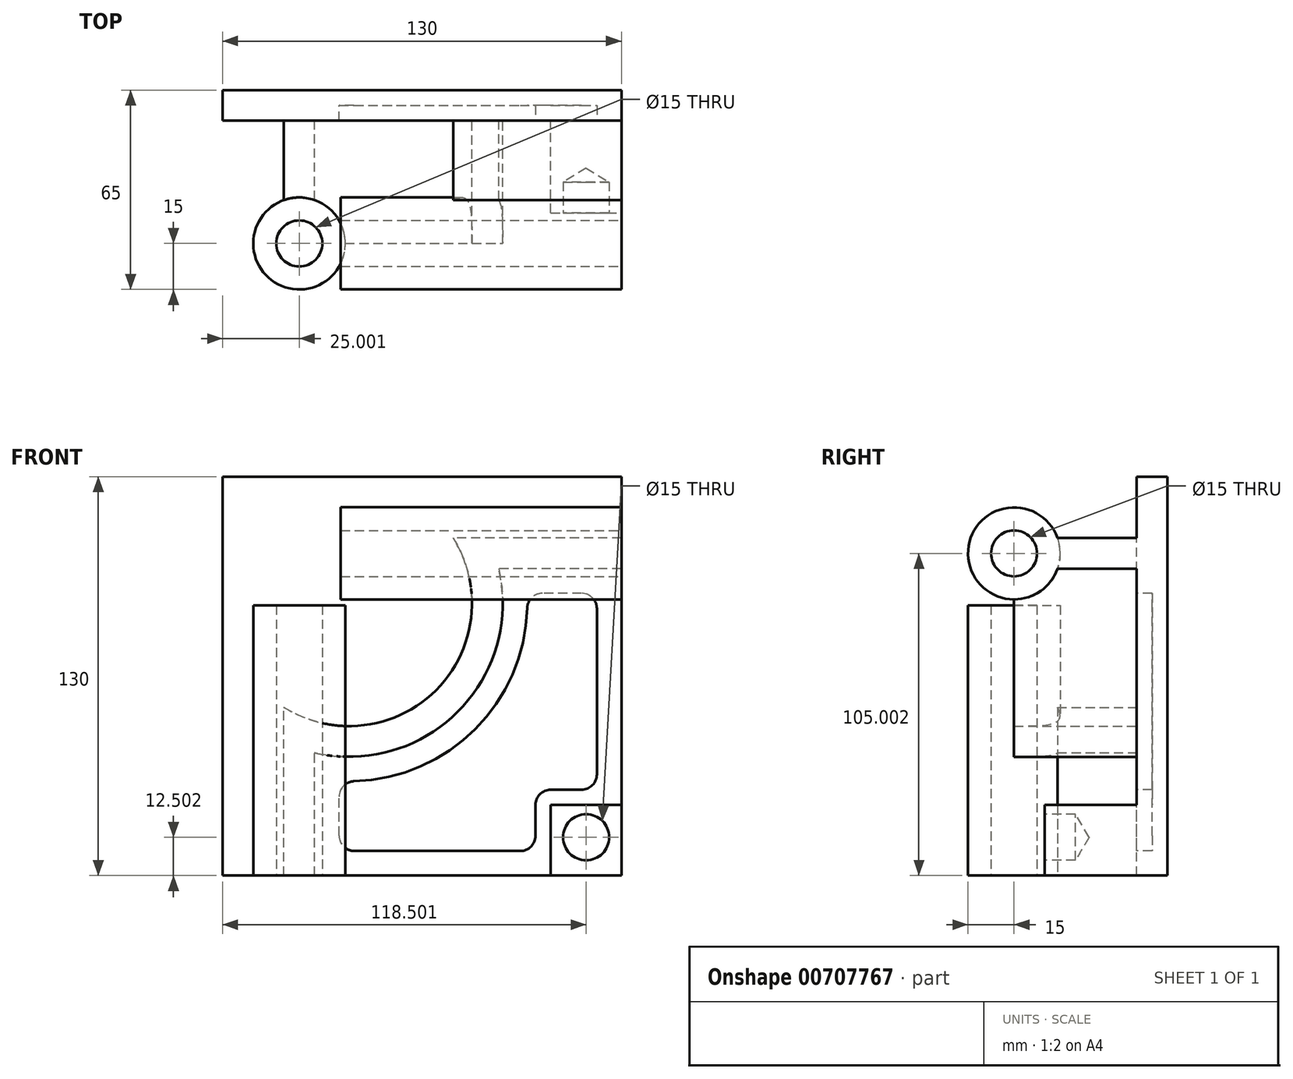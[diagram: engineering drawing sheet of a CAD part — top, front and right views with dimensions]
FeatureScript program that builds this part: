
annotation { "Feature Type Name" : "Feature", "Feature Type Description" : "" }
export const myFeature = defineFeature(function(context is Context, id is Id, definition is map)
    precondition{}
    {
        {
            var Q0;
            Q0=qCreatedBy(makeId("Front.planeOp"),FACE);
            var sketch = newSketch(context, id + "F0", { "sketchPlane" : qUnion([Q0])});
            skLineSegment(sketch, "E0.bottom", {"start": v(-59.9, 59.24) * mm, "end": v(70.1, 59.24) * mm});
            skLineSegment(sketch, "E0.top", {"start": v(-59.9, -70.76) * mm, "end": v(70.1, -70.76) * mm});
            skLineSegment(sketch, "E0.left", {"start": v(-59.9, 59.24) * mm, "end": v(-59.9, -70.76) * mm});
            skLineSegment(sketch, "E0.right", {"start": v(70.1, 59.24) * mm, "end": v(70.1, -70.76) * mm});
            skSolve(sketch);
        }
        {
            var Q0;
            Q0=makeQuery(id+"F0.imprint","IMPRINT",FACE,{"disambiguationData":[TD([[makeQuery(id+"F0.imprint","IMPRINT",EDGE,{"derivedFrom":sQuery(id+"F0.wireOp",EDGE,"E0.bottom")}),-1.0]])]});
            extrude(context, id + "F1", {"entities" : qUnion([Q0]), "depth" : 10 * mm, "offsetDistance" : 25 * mm});
        }
        {
            var Q0;
            Q0=makeQuery(id+"F1.opExtrude","CAP_FACE",FACE,{"disambiguationData":[OSD([sQuery(id+"F0.wireOp",EDGE,"E0.bottom"),sQuery(id+"F0.wireOp",EDGE,"E0.top"),sQuery(id+"F0.wireOp",EDGE,"E0.left"),sQuery(id+"F0.wireOp",EDGE,"E0.right")])],"isStart":false});
            var sketch = newSketch(context, id + "F2", { "sketchPlane" : qUnion([Q0])});
            skLineSegment(sketch, "E1", {"start": v(-29.9, -70.76) * mm, "end": v(-29.9, -30.76) * mm});
            skLineSegment(sketch, "E2", {"start": v(70.1, 29.24) * mm, "end": v(30.1, 29.24) * mm});
            skArc(sketch, "E3", {"start": v(-29.9, -30.76) * mm, "mid": v(16.74, -17.4) * mm, "end": v(30.1, 29.24) * mm});
            skLineSegment(sketch, "E4.0", {"start": v(70.1, 39.24) * mm, "end": v(15.25, 39.24) * mm});
            skArc(sketch, "E4.1", {"start": v(-39.9, -15.91) * mm, "mid": v(9.67, -10.33) * mm, "end": v(15.25, 39.24) * mm});
            skLineSegment(sketch, "E4.2", {"start": v(-39.9, -70.76) * mm, "end": v(-39.9, -15.91) * mm});
            skSolve(sketch);
        }
        {
            var Q0;
            Q0 = qSketchRegion(id + "F2", true);
            var Q1;
            {var subQ3=sQuery(id+"F2.wireOp",EDGE,"E1");Q1=makeQuery(id+"F2.imprint","IMPRINT",FACE,{"disambiguationData":[TD([[makeQuery(id+"F2.imprint","IMPRINT",EDGE,{"derivedFrom":subQ3}),1.0]])]});}
            extrude(context, id + "F3", {"entities" : qUnion([Q0, Q1]), "operationType" : NewBodyOperationType.ADD, "depth" : 40 * mm, "offsetDistance" : 25 * mm});
        }
        {
            var Q0;
            {var subQ0=sQuery(id+"F0.wireOp",EDGE,"E0.right");var subQ1=sQuery(id+"F0.wireOp",EDGE,"E0.top");Q0=makeQuery(id+"F3.boolean.opBoolean","SPLIT",FACE,{"disambiguationData":[TD([makeQuery(id+"F3.opExtrude","SWEPT_FACE",FACE,{"disambiguationData":[OSD([sQuery(id+"F2.wireOp",EDGE,"E1")])]})])],"derivedFrom":makeQuery(id+"F1.opExtrude","CAP_FACE",FACE,{"disambiguationData":[OSD([sQuery(id+"F0.wireOp",EDGE,"E0.bottom"),subQ1,sQuery(id+"F0.wireOp",EDGE,"E0.left"),subQ0])],"isStart":false})});}
            var sketch = newSketch(context, id + "F4", { "sketchPlane" : qUnion([Q0])});
            skLineSegment(sketch, "E5.0", {"start": v(70.1, 21.24) * mm, "end": v(39.29, 21.24) * mm});
            skArc(sketch, "E5.1", {"start": v(-21.9, -39.96) * mm, "mid": v(22.4, -23.06) * mm, "end": v(39.29, 21.24) * mm});
            skLineSegment(sketch, "E5.2", {"start": v(-21.9, -70.76) * mm, "end": v(-21.9, -39.96) * mm});
            skLineSegment(sketch, "E6", {"start": v(-21.9, -62.76) * mm, "end": v(70.1, -62.76) * mm});
            skLineSegment(sketch, "E7", {"start": v(62.1, 21.24) * mm, "end": v(62.1, -70.76) * mm});
            skLineSegment(sketch, "E8", {"start": v(42.1, -62.76) * mm, "end": v(42.1, -42.76) * mm});
            skLineSegment(sketch, "E9", {"start": v(42.1, -42.76) * mm, "end": v(62.1, -42.76) * mm});
            skSolve(sketch);
        }
        {
            var Q0;
            {var subQ4=sQuery(id+"F4.wireOp",EDGE,"E5.1");Q0=makeQuery(id+"F4.imprint","IMPRINT",FACE,{"disambiguationData":[TD([[makeQuery(id+"F4.imprint","IMPRINT",EDGE,{"derivedFrom":subQ4}),-1.0]])]});}
            extrude(context, id + "F5", {"entities" : qUnion([Q0]), "operationType" : NewBodyOperationType.REMOVE, "oppositeDirection" : true, "depth" : 5 * mm, "offsetDistance" : 25 * mm});
        }
        {
            var Q0;
            {var subQ0=sQuery(id+"F0.wireOp",EDGE,"E0.right");Q0=makeQuery(id+"F3.boolean.opBoolean","MERGE",FACE,{"derivedFrom":[makeQuery(id+"F1.opExtrude","SWEPT_FACE",FACE,{"disambiguationData":[OSD([subQ0])]}),makeQuery(id+"F3.opExtrude","SWEPT_FACE",FACE,{"disambiguationData":[OSD([subQ0])]})]});}
            var sketch = newSketch(context, id + "F6", { "sketchPlane" : qUnion([Q0])});
            skCircle(sketch, "E10", {"center": v(-50, 34.24) * mm, "radius": 15 * mm});
            skSolve(sketch);
        }
        {
            var Q0;
            {var subQ0=sQuery(id+"F6.wireOp",EDGE,"E10");var subQ1=sQuery(id+"F0.wireOp",EDGE,"E0.right");var subQ2=makeQuery(id+"F3.opExtrude","SWEPT_EDGE",EDGE,{"disambiguationData":[OSD([subQ1,sQuery(id+"F2.wireOp",EDGE,"E2")])]});var subQ3=makeQuery(id+"F6.imprint","INTERSECT",VERTEX,{"derivedFrom":[subQ2,subQ0]});Q0=makeQuery(id+"F6.imprint","IMPRINT",FACE,{"disambiguationData":[TD([[makeQuery(id+"F6.imprint","IMPRINT",EDGE,{"disambiguationData":[TD([[subQ3,1.0]])],"derivedFrom":subQ0}),1.0]])]});}
            var Q1;
            {var subQ0=sQuery(id+"F6.wireOp",EDGE,"E10");var subQ1=sQuery(id+"F0.wireOp",EDGE,"E0.right");var subQ2=makeQuery(id+"F3.opExtrude","SWEPT_EDGE",EDGE,{"disambiguationData":[OSD([subQ1,sQuery(id+"F2.wireOp",EDGE,"E2")])]});var subQ3=makeQuery(id+"F6.imprint","INTERSECT",VERTEX,{"derivedFrom":[subQ2,subQ0]});Q1=makeQuery(id+"F6.imprint","IMPRINT",FACE,{"disambiguationData":[TD([[makeQuery(id+"F6.imprint","IMPRINT",EDGE,{"disambiguationData":[TD([[subQ3,-1.0]])],"derivedFrom":subQ0}),1.0]])]});}
            extrude(context, id + "F7", {"entities" : qUnion([Q0, Q1]), "operationType" : NewBodyOperationType.ADD, "oppositeDirection" : true, "depth" : 91.5 * mm, "offsetDistance" : 25 * mm});
        }
        {
            var Q0;
            {var subQ0=sQuery(id+"F0.wireOp",EDGE,"E0.right");Q0=makeQuery(id+"F7.boolean.opBoolean","MERGE",FACE,{"derivedFrom":[makeQuery(id+"F3.boolean.opBoolean","MERGE",FACE,{"derivedFrom":[makeQuery(id+"F1.opExtrude","SWEPT_FACE",FACE,{"disambiguationData":[OSD([subQ0])]}),makeQuery(id+"F3.opExtrude","SWEPT_FACE",FACE,{"disambiguationData":[OSD([subQ0])]})]}),makeQuery(id+"F7.opExtrude","CAP_FACE",FACE,{"disambiguationData":[OSD([sQuery(id+"F6.wireOp",EDGE,"E10")])],"isStart":true})]});}
            var sketch = newSketch(context, id + "F8", { "sketchPlane" : qUnion([Q0])});
            skCircle(sketch, "E11", {"center": v(-50, 34.24) * mm, "radius": 7.5 * mm});
            skSolve(sketch);
        }
        {
            var Q0;
            Q0=makeQuery(id+"F8.imprint","IMPRINT",FACE,{"disambiguationData":[TD([[makeQuery(id+"F8.imprint","IMPRINT",EDGE,{"derivedFrom":sQuery(id+"F8.wireOp",EDGE,"E11")}),1.0]])]});
            extrude(context, id + "F9", {"entities" : qUnion([Q0]), "operationType" : NewBodyOperationType.REMOVE, "oppositeDirection" : true, "depth" : 113 * mm, "offsetDistance" : 25 * mm});
        }
        {
            var Q0;
            {var subQ0=sQuery(id+"F0.wireOp",EDGE,"E0.top");Q0=makeQuery(id+"F3.boolean.opBoolean","MERGE",FACE,{"derivedFrom":[makeQuery(id+"F1.opExtrude","SWEPT_FACE",FACE,{"disambiguationData":[OSD([subQ0])]}),makeQuery(id+"F3.opExtrude","SWEPT_FACE",FACE,{"disambiguationData":[OSD([subQ0])]})]});}
            var sketch = newSketch(context, id + "F10", { "sketchPlane" : qUnion([Q0])});
            skCircle(sketch, "E12", {"center": v(-34.9, 50) * mm, "radius": 15 * mm});
            skCircle(sketch, "E13", {"center": v(-34.9, 50) * mm, "radius": 7.5 * mm});
            skSolve(sketch);
        }
        {
            var Q0;
            {var subQ0=sQuery(id+"F10.wireOp",EDGE,"E12");var subQ1=sQuery(id+"F0.wireOp",EDGE,"E0.top");var subQ2=makeQuery(id+"F3.opExtrude","SWEPT_EDGE",EDGE,{"disambiguationData":[OSD([subQ1,sQuery(id+"F2.wireOp",EDGE,"E1")])]});var subQ3=makeQuery(id+"F10.imprint","INTERSECT",VERTEX,{"derivedFrom":[subQ2,subQ0]});Q0=makeQuery(id+"F10.imprint","IMPRINT",FACE,{"disambiguationData":[TD([[makeQuery(id+"F10.imprint","IMPRINT",EDGE,{"disambiguationData":[TD([[subQ3,-1.0]])],"derivedFrom":subQ0}),1.0]])]});}
            var Q1;
            {var subQ0=sQuery(id+"F10.wireOp",EDGE,"E12");var subQ1=sQuery(id+"F0.wireOp",EDGE,"E0.top");var subQ2=makeQuery(id+"F3.opExtrude","SWEPT_EDGE",EDGE,{"disambiguationData":[OSD([subQ1,sQuery(id+"F2.wireOp",EDGE,"E1")])]});var subQ3=makeQuery(id+"F10.imprint","INTERSECT",VERTEX,{"derivedFrom":[subQ2,subQ0]});Q1=makeQuery(id+"F10.imprint","IMPRINT",FACE,{"disambiguationData":[TD([[makeQuery(id+"F10.imprint","IMPRINT",EDGE,{"disambiguationData":[TD([[subQ3,1.0]])],"derivedFrom":subQ0}),1.0]])]});}
            extrude(context, id + "F11", {"entities" : qUnion([Q0, Q1]), "operationType" : NewBodyOperationType.ADD, "oppositeDirection" : true, "depth" : 88 * mm, "offsetDistance" : 25 * mm});
        }
        {
            var Q0;
            {var subQ0=sQuery(id+"F0.wireOp",EDGE,"E0.top");Q0=makeQuery(id+"F11.boolean.opBoolean","MERGE",FACE,{"derivedFrom":[makeQuery(id+"F3.boolean.opBoolean","MERGE",FACE,{"derivedFrom":[makeQuery(id+"F1.opExtrude","SWEPT_FACE",FACE,{"disambiguationData":[OSD([subQ0])]}),makeQuery(id+"F3.opExtrude","SWEPT_FACE",FACE,{"disambiguationData":[OSD([subQ0])]})]}),makeQuery(id+"F11.opExtrude","CAP_FACE",FACE,{"disambiguationData":[OSD([sQuery(id+"F10.wireOp",EDGE,"E12"),sQuery(id+"F10.wireOp",EDGE,"E13")])],"isStart":true})]});}
            var sketch = newSketch(context, id + "F12", { "sketchPlane" : qUnion([Q0])});
            skCircle(sketch, "E14", {"center": v(-34.9, 50) * mm, "radius": 7.5 * mm});
            skLineSegment(sketch, "E15", {"start": v(-39.9, 44.4) * mm, "end": v(-39.9, 50) * mm});
            skLineSegment(sketch, "E16", {"start": v(-39.9, 50) * mm, "end": v(-29.9, 50) * mm});
            skLineSegment(sketch, "E17", {"start": v(-29.9, 50) * mm, "end": v(-29.9, 44.4) * mm});
            skSolve(sketch);
        }
        {
            var Q0;
            {var subQ2=sQuery(id+"F12.wireOp",EDGE,"E15");Q0=makeQuery(id+"F12.imprint","IMPRINT",FACE,{"disambiguationData":[TD([[makeQuery(id+"F12.imprint","IMPRINT",EDGE,{"derivedFrom":subQ2}),1.0]])]});}
            extrude(context, id + "F13", {"entities" : qUnion([Q0]), "operationType" : NewBodyOperationType.REMOVE, "oppositeDirection" : true, "depth" : 90.4 * mm, "offsetDistance" : 25 * mm});
        }
        {
            var Q0;
            {var subQ0=sQuery(id+"F0.wireOp",EDGE,"E0.top");Q0=makeQuery(id+"F11.boolean.opBoolean","MERGE",FACE,{"derivedFrom":[makeQuery(id+"F3.boolean.opBoolean","MERGE",FACE,{"derivedFrom":[makeQuery(id+"F1.opExtrude","SWEPT_FACE",FACE,{"disambiguationData":[OSD([subQ0])]}),makeQuery(id+"F3.opExtrude","SWEPT_FACE",FACE,{"disambiguationData":[OSD([subQ0])]})]}),makeQuery(id+"F11.opExtrude","CAP_FACE",FACE,{"disambiguationData":[OSD([sQuery(id+"F10.wireOp",EDGE,"E12"),sQuery(id+"F10.wireOp",EDGE,"E13")])],"isStart":true})]});}
            var sketch = newSketch(context, id + "F14", { "sketchPlane" : qUnion([Q0])});
            skCircle(sketch, "E18", {"center": v(-34.9, 50) * mm, "radius": 7.5 * mm});
            skLineSegment(sketch, "E19", {"start": v(-29.95, 44.38) * mm, "end": v(-29.95, 50.3) * mm});
            skLineSegment(sketch, "E20", {"start": v(-29.95, 50.3) * mm, "end": v(-27.41, 50.3) * mm});
            skSolve(sketch);
        }
        {
            var Q0;
            {var subQ0=sQuery(id+"F14.wireOp",EDGE,"E19");Q0=makeQuery(id+"F14.imprint","IMPRINT",FACE,{"disambiguationData":[TD([[makeQuery(id+"F14.imprint","IMPRINT",EDGE,{"derivedFrom":subQ0}),-1.0]])]});}
            extrude(context, id + "F15", {"entities" : qUnion([Q0]), "operationType" : NewBodyOperationType.REMOVE, "oppositeDirection" : true, "depth" : 100.3 * mm, "offsetDistance" : 25 * mm});
        }
        {
            var Q0;
            {var subQ0=sQuery(id+"F0.wireOp",EDGE,"E0.right");var subQ1=sQuery(id+"F0.wireOp",EDGE,"E0.top");Q0=makeQuery(id+"F3.boolean.opBoolean","SPLIT",FACE,{"disambiguationData":[TD([makeQuery(id+"F3.opExtrude","SWEPT_FACE",FACE,{"disambiguationData":[OSD([sQuery(id+"F2.wireOp",EDGE,"E1")])]})])],"derivedFrom":makeQuery(id+"F1.opExtrude","CAP_FACE",FACE,{"disambiguationData":[OSD([sQuery(id+"F0.wireOp",EDGE,"E0.bottom"),subQ1,sQuery(id+"F0.wireOp",EDGE,"E0.left"),subQ0])],"isStart":false})});}
            var sketch = newSketch(context, id + "F16", { "sketchPlane" : qUnion([Q0])});
            skLineSegment(sketch, "E21.bottom", {"start": v(70.1, -70.76) * mm, "end": v(47.1, -70.76) * mm});
            skLineSegment(sketch, "E21.top", {"start": v(70.1, -47.76) * mm, "end": v(47.1, -47.76) * mm});
            skLineSegment(sketch, "E21.left", {"start": v(70.1, -70.76) * mm, "end": v(70.1, -47.76) * mm});
            skLineSegment(sketch, "E21.right", {"start": v(47.1, -70.76) * mm, "end": v(47.1, -47.76) * mm});
            skSolve(sketch);
        }
        {
            var Q0;
            Q0=makeQuery(id+"F16.imprint","IMPRINT",FACE,{"disambiguationData":[TD([[makeQuery(id+"F16.imprint","IMPRINT",EDGE,{"derivedFrom":sQuery(id+"F16.wireOp",EDGE,"E21.bottom")}),1.0]])]});
            extrude(context, id + "F17", {"entities" : qUnion([Q0]), "operationType" : NewBodyOperationType.ADD, "depth" : 30 * mm, "offsetDistance" : 25 * mm});
        }
        {
            var Q0;
            Q0=makeQuery(id+"F17.opExtrude","CAP_FACE",FACE,{"disambiguationData":[OSD([sQuery(id+"F16.wireOp",EDGE,"E21.bottom"),sQuery(id+"F16.wireOp",EDGE,"E21.top"),sQuery(id+"F16.wireOp",EDGE,"E21.left"),sQuery(id+"F16.wireOp",EDGE,"E21.right")])],"isStart":false});
            var sketch = newSketch(context, id + "F18", { "sketchPlane" : qUnion([Q0])});
            skCircle(sketch, "E22", {"center": v(58.6, -58.26) * mm, "radius": 7.5 * mm});
            skPoint(sketch, "E22.centerSnap0", {"position": v(58.6, -70.76) * mm});
            skSolve(sketch);
        }
        {
            var Q0;
            Q0=sQuery(id+"F18.wireOp",VERTEX,"E22.center");
            var Q1;
            Q1=makeQuery(id+"F1.opExtrude","SWEPT_BODY",BODY,{"disambiguationData":[OSD([sQuery(id+"F0.wireOp",EDGE,"E0.bottom"),sQuery(id+"F0.wireOp",EDGE,"E0.top"),sQuery(id+"F0.wireOp",EDGE,"E0.left"),sQuery(id+"F0.wireOp",EDGE,"E0.right")])]});
            hole(context, id + "F19", {"style" : HoleStyle.SIMPLE, "endStyle" : HoleEndStyle.BLIND, "holeDiameter" : 15 * mm, "majorDiameter" : 5 * mm, "holeDepth" : 10 * mm, "isTappedThrough" : true, "tappedDepth" : 12 * mm, "tapClearance" : 3, "locations" : qUnion([Q0]), "scope" : qUnion([Q1])});
        }
        {
            var Q0;
            Q0=makeQuery(id+"F5.boolean.opBoolean","COPY",EDGE,{"derivedFrom":makeQuery(id+"F5.opExtrude","SWEPT_EDGE",EDGE,{"disambiguationData":[OSD([sQuery(id+"F4.wireOp",EDGE,"E8"),sQuery(id+"F4.wireOp",EDGE,"E9")])]})});
            fillet(context, id + "F20", {"entities" : qUnion([Q0]), "radius" : 5 * mm, "tangentPropagation" : true, "allowEdgeOverflow" : false});
        }
        {
            var Q0;
            Q0=makeQuery(id+"F5.boolean.opBoolean","COPY",EDGE,{"derivedFrom":makeQuery(id+"F5.opExtrude","SWEPT_EDGE",EDGE,{"disambiguationData":[OSD([sQuery(id+"F4.wireOp",EDGE,"E7"),sQuery(id+"F4.wireOp",EDGE,"E9")])]})});
            fillet(context, id + "F21", {"entities" : qUnion([Q0]), "radius" : 5 * mm, "tangentPropagation" : true, "allowEdgeOverflow" : false});
        }
        {
            var Q0;
            Q0=makeQuery(id+"F5.boolean.opBoolean","COPY",EDGE,{"derivedFrom":makeQuery(id+"F5.opExtrude","SWEPT_EDGE",EDGE,{"disambiguationData":[OSD([sQuery(id+"F4.wireOp",EDGE,"E6"),sQuery(id+"F4.wireOp",EDGE,"E8")])]})});
            fillet(context, id + "F22", {"entities" : qUnion([Q0]), "radius" : 5 * mm, "tangentPropagation" : true, "allowEdgeOverflow" : false});
        }
        {
            var Q0;
            Q0=makeQuery(id+"F5.boolean.opBoolean","COPY",EDGE,{"derivedFrom":makeQuery(id+"F5.opExtrude","SWEPT_EDGE",EDGE,{"disambiguationData":[OSD([sQuery(id+"F4.wireOp",EDGE,"E5.2"),sQuery(id+"F4.wireOp",EDGE,"E6")])]})});
            fillet(context, id + "F23", {"entities" : qUnion([Q0]), "radius" : 5 * mm, "tangentPropagation" : true, "allowEdgeOverflow" : false});
        }
        {
            var Q0;
            Q0=makeQuery(id+"F5.boolean.opBoolean","COPY",EDGE,{"derivedFrom":makeQuery(id+"F5.opExtrude","SWEPT_EDGE",EDGE,{"disambiguationData":[OSD([sQuery(id+"F4.wireOp",EDGE,"E5.0"),sQuery(id+"F4.wireOp",EDGE,"E7")])]})});
            fillet(context, id + "F24", {"entities" : qUnion([Q0]), "radius" : 5 * mm, "tangentPropagation" : true, "allowEdgeOverflow" : false});
        }
        {
            var Q0;
            Q0=makeQuery(id+"F5.boolean.opBoolean","COPY",EDGE,{"derivedFrom":makeQuery(id+"F5.opExtrude","SWEPT_EDGE",EDGE,{"disambiguationData":[OSD([sQuery(id+"F4.wireOp",EDGE,"E5.0"),sQuery(id+"F4.wireOp",EDGE,"E5.1")])]})});
            fillet(context, id + "F25", {"entities" : qUnion([Q0]), "radius" : 5 * mm, "tangentPropagation" : true, "allowEdgeOverflow" : false});
        }
        {
            var Q0;
            Q0=makeQuery(id+"F5.boolean.opBoolean","COPY",EDGE,{"derivedFrom":makeQuery(id+"F5.opExtrude","SWEPT_EDGE",EDGE,{"disambiguationData":[OSD([sQuery(id+"F4.wireOp",EDGE,"E5.1"),sQuery(id+"F4.wireOp",EDGE,"E5.2")])]})});
            fillet(context, id + "F26", {"entities" : qUnion([Q0]), "radius" : 5 * mm, "tangentPropagation" : true, "allowEdgeOverflow" : false});
        }
    });
